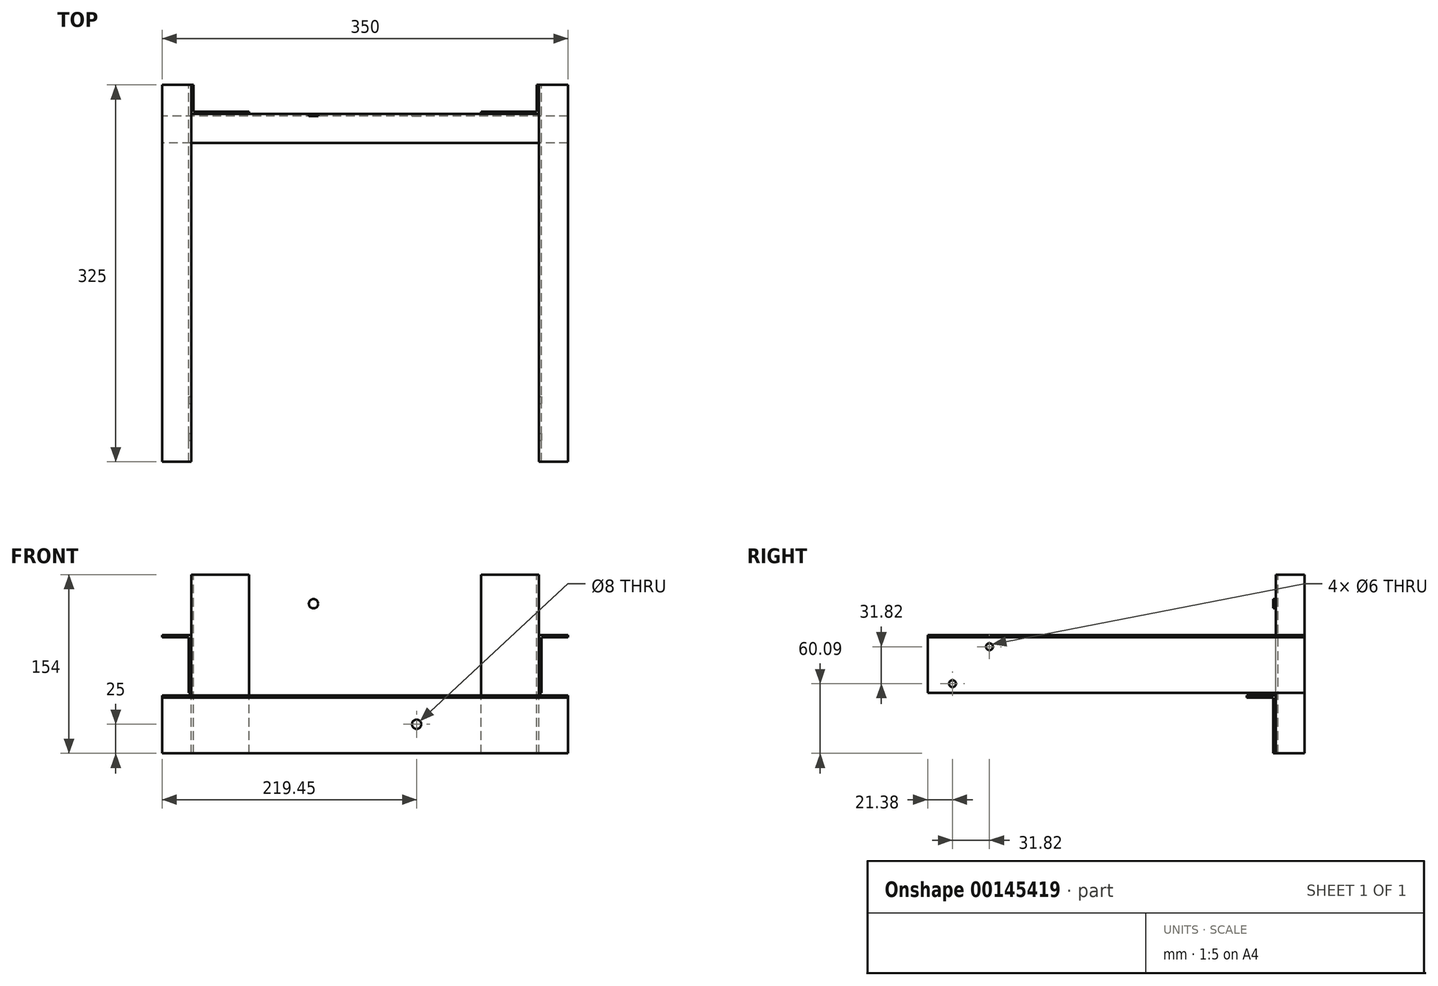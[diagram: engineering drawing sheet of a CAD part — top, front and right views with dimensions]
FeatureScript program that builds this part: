
annotation { "Feature Type Name" : "Feature", "Feature Type Description" : "" }
export const myFeature = defineFeature(function(context is Context, id is Id, definition is map)
    precondition{}
    {
        {
            var Q0;
            Q0=qCreatedBy(makeId("Right.planeOp"),FACE);
            var sketch = newSketch(context, id + "F0", { "sketchPlane" : qUnion([Q0])});
            skLineSegment(sketch, "E0", {"start": v(0, 0) * mm, "end": v(0, -50) * mm});
            skLineSegment(sketch, "E1", {"start": v(0, -50) * mm, "end": v(0, -104) * mm});
            skLineSegment(sketch, "E2", {"start": v(0, -104) * mm, "end": v(-25, -104) * mm});
            skLineSegment(sketch, "E3", {"start": v(-25, -104) * mm, "end": v(-25, -106) * mm});
            skLineSegment(sketch, "E4", {"start": v(0, -104) * mm, "end": v(0, -154) * mm});
            skLineSegment(sketch, "E5.0", {"start": v(-2, -106) * mm, "end": v(-2, -154) * mm});
            skLineSegment(sketch, "E6", {"start": v(-25, -106) * mm, "end": v(-2, -106) * mm});
            skLineSegment(sketch, "E7", {"start": v(0, -154) * mm, "end": v(-2, -154) * mm});
            skLineSegment(sketch, "E8", {"start": v(0, -50) * mm, "end": v(-25, -50) * mm});
            skLineSegment(sketch, "E9", {"start": v(-25, -50) * mm, "end": v(-25, -48) * mm});
            skLineSegment(sketch, "E10", {"start": v(-25, -48) * mm, "end": v(-2, -48) * mm});
            skLineSegment(sketch, "E11", {"start": v(-2, -48) * mm, "end": v(-2, 0) * mm});
            skLineSegment(sketch, "E12", {"start": v(0, 0) * mm, "end": v(-2, 0) * mm});
            skSolve(sketch);
        }
        {
            var Q0;
            Q0 = qSketchRegion(id + "F0", true);
            extrude(context, id + "F1", {"entities" : qUnion([Q0]), "depth" : 350 * mm, "symmetric" : true});
        }
        {
            var Q0;
            Q0=qCreatedBy(makeId("Front.planeOp"),FACE);
            var sketch = newSketch(context, id + "F2", { "sketchPlane" : qUnion([Q0])});
            skLineSegment(sketch, "E13.0", {"start": v(175, 0) * mm, "end": v(175, -2) * mm});
            skLineSegment(sketch, "E14", {"start": v(150, -52) * mm, "end": v(150, -102) * mm});
            skLineSegment(sketch, "E15.1", {"start": v(152, -54) * mm, "end": v(152, -102) * mm});
            skLineSegment(sketch, "E15.2", {"start": v(175, -54) * mm, "end": v(152, -54) * mm});
            skLineSegment(sketch, "E16", {"start": v(150, -52) * mm, "end": v(175, -52) * mm});
            skLineSegment(sketch, "E17", {"start": v(175, -2) * mm, "end": v(175, -54) * mm});
            skLineSegment(sketch, "E18.MirrorCS", {"start": v(-175, 0) * mm, "end": v(-175, -2) * mm});
            skLineSegment(sketch, "E19.MirrorCS", {"start": v(-175, -2) * mm, "end": v(-175, -54) * mm});
            skLineSegment(sketch, "E20.MirrorCS", {"start": v(-150, -52) * mm, "end": v(-150, -102) * mm});
            skLineSegment(sketch, "E21.MirrorCS", {"start": v(-175, -54) * mm, "end": v(-152, -54) * mm});
            skLineSegment(sketch, "E22.MirrorCS", {"start": v(-150, -52) * mm, "end": v(-175, -52) * mm});
            skLineSegment(sketch, "E23.MirrorCS", {"start": v(-152, -54) * mm, "end": v(-152, -102) * mm});
            skLineSegment(sketch, "E24", {"start": v(150, -102) * mm, "end": v(152, -102) * mm});
            skLineSegment(sketch, "E25", {"start": v(-150, -102) * mm, "end": v(-152, -102) * mm});
            skSolve(sketch);
        }
        {
            var Q0;
            Q0 = qSketchRegion(id + "F2", true);
            extrude(context, id + "F3", {"entities" : qUnion([Q0]), "depth" : 300 * mm, "hasSecondDirection" : true, "secondDirectionOppositeDirection" : true, "secondDirectionDepth" : 25 * mm});
        }
        {
            var Q0;
            Q0=qCreatedBy(makeId("Top.planeOp"),FACE);
            var sketch = newSketch(context, id + "F4", { "sketchPlane" : qUnion([Q0])});
            skLineSegment(sketch, "E26", {"start": v(150, 0) * mm, "end": v(100, 0) * mm});
            skLineSegment(sketch, "E27", {"start": v(150, 0) * mm, "end": v(150, 25) * mm});
            skLineSegment(sketch, "E28.1", {"start": v(148, 2) * mm, "end": v(100, 2) * mm});
            skLineSegment(sketch, "E28.2", {"start": v(148, 2) * mm, "end": v(148, 25) * mm});
            skLineSegment(sketch, "E29", {"start": v(150, 25) * mm, "end": v(148, 25) * mm});
            skLineSegment(sketch, "E30.MirrorCS", {"start": v(-150, 25) * mm, "end": v(-148, 25) * mm});
            skPoint(sketch, "E31.MirrorP", {"position": v(-150, 0) * mm});
            skLineSegment(sketch, "E32.MirrorCS", {"start": v(-148, 2) * mm, "end": v(-148, 25) * mm});
            skLineSegment(sketch, "E33.MirrorCS", {"start": v(-148, 2) * mm, "end": v(-100, 2) * mm});
            skLineSegment(sketch, "E34.MirrorCS", {"start": v(-150, 0) * mm, "end": v(-150, 25) * mm});
            skLineSegment(sketch, "E35.MirrorCS", {"start": v(-150, 0) * mm, "end": v(-100, 0) * mm});
            skLineSegment(sketch, "E36", {"start": v(100, 0) * mm, "end": v(100, 2) * mm});
            skLineSegment(sketch, "E37", {"start": v(-100, 0) * mm, "end": v(-100, 2) * mm});
            skSolve(sketch);
        }
        {
            var Q0;
            Q0 = qSketchRegion(id + "F4", true);
            extrude(context, id + "F5", {"entities" : qUnion([Q0]), "oppositeDirection" : true, "depth" : 154 * mm});
        }
        {
            var Q0;
            Q0=makeQuery(id+"F1.opExtrude","SWEPT_FACE",FACE,{"disambiguationData":[OSD([sQuery(id+"F0.wireOp",EDGE,"E0")])]});
            var sketch = newSketch(context, id + "F6", { "sketchPlane" : qUnion([Q0])});
            skCircle(sketch, "E38", {"center": v(-44.45, -25) * mm, "radius": 4 * mm});
            skCircle(sketch, "E39.MirrorC", {"center": v(44.45, -25) * mm, "radius": 4 * mm});
            skCircle(sketch, "E40", {"center": v(-44.45, -129) * mm, "radius": 4 * mm});
            skLineSegment(sketch, "E41", {"start": v(0, 0) * mm, "end": v(0, -157.33) * mm, "construction": true});
            skCircle(sketch, "E42.MirrorC", {"center": v(44.45, -129) * mm, "radius": 4 * mm});
            skSolve(sketch);
        }
        {
            var Q0;
            Q0=makeQuery(id+"F6.imprint","IMPRINT",FACE,{"disambiguationData":[TD([[makeQuery(id+"F6.imprint","IMPRINT",EDGE,{"derivedFrom":sQuery(id+"F6.wireOp",EDGE,"E38")}),1.0]])]});
            var Q1;
            Q1=makeQuery(id+"F6.imprint","IMPRINT",FACE,{"disambiguationData":[TD([[makeQuery(id+"F6.imprint","IMPRINT",EDGE,{"derivedFrom":sQuery(id+"F6.wireOp",EDGE,"E39.MirrorC")}),-1.0]])]});
            var Q2;
            Q2=makeQuery(id+"F6.imprint","IMPRINT",FACE,{"disambiguationData":[TD([[makeQuery(id+"F6.imprint","IMPRINT",EDGE,{"derivedFrom":sQuery(id+"F6.wireOp",EDGE,"E40")}),1.0]])]});
            var Q3;
            Q3=makeQuery(id+"F6.imprint","IMPRINT",FACE,{"disambiguationData":[TD([[makeQuery(id+"F6.imprint","IMPRINT",EDGE,{"derivedFrom":sQuery(id+"F6.wireOp",EDGE,"E42.MirrorC")}),-1.0]])]});
            extrude(context, id + "F7", {"entities" : qUnion([Q0, Q1, Q2, Q3]), "operationType" : NewBodyOperationType.REMOVE, "oppositeDirection" : true, "depth" : 25 * mm});
        }
        {
            var Q0;
            Q0=makeQuery(id+"F3.opExtrude","SWEPT_FACE",FACE,{"disambiguationData":[OSD([sQuery(id+"F2.wireOp",EDGE,"E15.1")])]});
            var sketch = newSketch(context, id + "F8", { "sketchPlane" : qUnion([Q0])});
            skLineSegment(sketch, "E43.bottom", {"start": v(-238.71, -102) * mm, "end": v(-286.71, -102) * mm, "construction": true});
            skLineSegment(sketch, "E43.top", {"start": v(-238.71, -54) * mm, "end": v(-286.71, -54) * mm, "construction": true});
            skLineSegment(sketch, "E43.left", {"start": v(-238.71, -102) * mm, "end": v(-238.71, -54) * mm, "construction": true});
            skLineSegment(sketch, "E43.right", {"start": v(-286.71, -102) * mm, "end": v(-286.71, -54) * mm, "construction": true});
            skPoint(sketch, "E43.middle", {"position": v(-262.71, -78) * mm});
            skPoint(sketch, "E43.middle.positionSnap0", {"position": v(-300, -78) * mm});
            skPoint(sketch, "E43.centerSnap0", {"position": v(-300, -78) * mm});
            skLineSegment(sketch, "E44", {"start": v(-286.71, -102) * mm, "end": v(-238.71, -54) * mm});
            skCircle(sketch, "E45", {"center": v(-246.8, -62.1) * mm, "radius": 3 * mm});
            skCircle(sketch, "E46", {"center": v(-278.62, -93.9) * mm, "radius": 3 * mm});
            skSolve(sketch);
        }
        {
            var Q0;
            Q0 = qSketchRegion(id + "F8", true);
            extrude(context, id + "F9", {"entities" : qUnion([Q0]), "operationType" : NewBodyOperationType.REMOVE, "oppositeDirection" : true, "depth" : 400 * mm});
        }
    });
